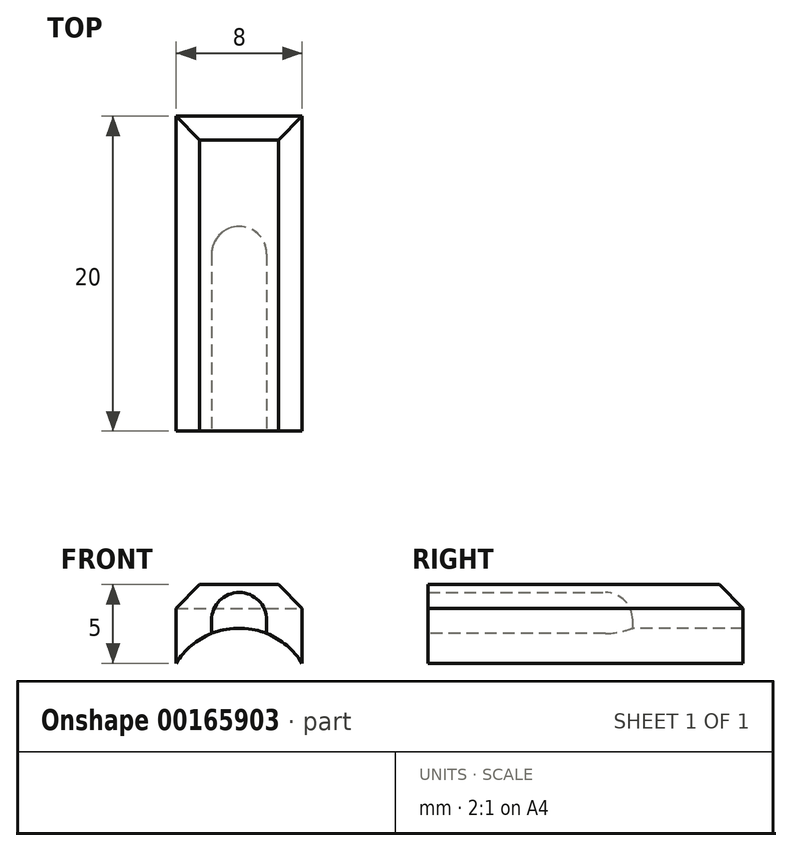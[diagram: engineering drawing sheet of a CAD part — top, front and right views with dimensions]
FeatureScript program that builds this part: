
annotation { "Feature Type Name" : "Feature", "Feature Type Description" : "" }
export const myFeature = defineFeature(function(context is Context, id is Id, definition is map)
    precondition{}
    {
        {
            assignVariable(context, id + "F0", {"name" : "Main_Length", "anyValue" : 20});
        }
        {
            assignVariable(context, id + "F1", {"name" : "Bore_Diam", "anyValue" : 3.5});
        }
        {
            assignVariable(context, id + "F2", {"name" : "Bore_Offset", "anyValue" : 0.5});
        }
        {
            assignVariable(context, id + "F3", {"name" : "Chamfer", "anyValue" : 1.5});
        }
        {
            var Q0;
            Q0=qCreatedBy(makeId("Front.planeOp"),FACE);
            var sketch = newSketch(context, id + "F4", { "sketchPlane" : qUnion([Q0])});
            skArc(sketch, "E0", {"start": v(4, 2.47) * mm, "mid": v(0, 4.7) * mm, "end": v(-4, 2.47) * mm});
            skLineSegment(sketch, "E1.bottom", {"start": v(4, 7.47) * mm, "end": v(-4, 7.47) * mm});
            skLineSegment(sketch, "E1.left", {"start": v(4, 7.47) * mm, "end": v(4, 2.47) * mm});
            skLineSegment(sketch, "E1.right", {"start": v(-4, 7.47) * mm, "end": v(-4, 2.47) * mm});
            skPoint(sketch, "E1.middle", {"position": v(0, 4.97) * mm});
            skArc(sketch, "E2", {"start": v(1.75, 5.22) * mm, "mid": v(0, 6.97) * mm, "end": v(-1.75, 5.22) * mm});
            skLineSegment(sketch, "E3", {"start": v(-1.75, 5.22) * mm, "end": v(-1.75, 4.36) * mm});
            skLineSegment(sketch, "E4", {"start": v(1.75, 5.22) * mm, "end": v(1.75, 4.36) * mm});
            skSolve(sketch);
        }
        {
            var Q0;
            Q0=makeQuery(id+"F4.imprint","IMPRINT",FACE,{"disambiguationData":[TD([[makeQuery(id+"F4.imprint","IMPRINT",EDGE,{"derivedFrom":sQuery(id+"F4.wireOp",EDGE,"E0")}),-1.0]])]});
            var Q1;
            {var subQ0=sQuery(id+"F4.wireOp",EDGE,"E2");var subQ1=sQuery(id+"F4.wireOp",EDGE,"E0");var subQ2=makeQuery(id+"F4.imprint","INTERSECT",VERTEX,{"disambiguationData":[OD(0.0)],"derivedFrom":[subQ1,subQ0]});Q1=makeQuery(id+"F4.imprint","IMPRINT",FACE,{"disambiguationData":[TD([[makeQuery(id+"F4.imprint","IMPRINT",EDGE,{"disambiguationData":[TD([[subQ2,-1.0]])],"derivedFrom":subQ1}),-1.0]])]});}
            var Q2;
            Q2=makeQuery(id+"F4.imprint","IMPRINT",FACE,{"disambiguationData":[TD([[makeQuery(id+"F4.imprint","IMPRINT",EDGE,{"derivedFrom":sQuery(id+"F4.wireOp",EDGE,"E2")}),1.0]])]});
            extrude(context, id + "F5", {"entities" : qUnion([Q0, Q1, Q2]), "oppositeDirection" : true, "depth" : (getVariable(context, 'Main_Length')) * mm});
        }
        {
            var Q0;
            Q0=makeQuery(id+"F5.opExtrude","SWEPT_EDGE",EDGE,{"disambiguationData":[OSD([sQuery(id+"F4.wireOp",EDGE,"E1.bottom"),sQuery(id+"F4.wireOp",EDGE,"E1.right")])]});
            var Q1;
            Q1=makeQuery(id+"F5.opExtrude","SWEPT_EDGE",EDGE,{"disambiguationData":[OSD([sQuery(id+"F4.wireOp",EDGE,"E1.bottom"),sQuery(id+"F4.wireOp",EDGE,"E1.left")])]});
            chamfer(context, id + "F6", {"entities" : qUnion([Q0, Q1]), "width" : (getVariable(context, 'Chamfer')) * mm, "tangentPropagation" : true});
        }
        {
            var Q0;
            Q0=makeQuery(id+"F5.opExtrude","CAP_EDGE",EDGE,{"disambiguationData":[OSD([sQuery(id+"F4.wireOp",EDGE,"E1.bottom")])],"isStart":false});
            chamfer(context, id + "F7", {"entities" : qUnion([Q0]), "width" : 1.5 * mm, "tangentPropagation" : true});
        }
        {
            var Q0;
            Q0=makeQuery(id+"F5.opExtrude","SWEPT_FACE",FACE,{"disambiguationData":[OSD([sQuery(id+"F4.wireOp",EDGE,"E1.bottom")])]});
            cPlane(context, id + "F8", {"entities" : qUnion([Q0]), "cplaneType" : CPlaneType.OFFSET, "offset" : (getVariable(context, 'Bore_Offset') + getVariable(context, 'Bore_Diam') / 2) * mm, "oppositeDirection" : true, "width" : 150 * mm, "height" : 150 * mm});
        }
        {
            var Q0;
            Q0=qCreatedBy(id+"F8.planeOp",FACE);
            var sketch = newSketch(context, id + "F9", { "sketchPlane" : qUnion([Q0])});
            skLineSegment(sketch, "E5", {"start": v(-1.75, 0) * mm, "end": v(-1.75, 11.25) * mm});
            skLineSegment(sketch, "E6", {"start": v(1.75, 0) * mm, "end": v(1.75, 11.25) * mm});
            skArc(sketch, "E7", {"start": v(1.75, 11.25) * mm, "mid": v(0, 13) * mm, "end": v(-1.75, 11.25) * mm});
            skLineSegment(sketch, "E8", {"start": v(-1.75, 0) * mm, "end": v(1.75, 0) * mm});
            skLineSegment(sketch, "E9", {"start": v(0, 0) * mm, "end": v(0, 13) * mm});
            skSolve(sketch);
        }
        {
            var Q0;
            {var subQ0=sQuery(id+"F9.wireOp",EDGE,"E5");Q0=makeQuery(id+"F9.imprint","IMPRINT",FACE,{"disambiguationData":[TD([[makeQuery(id+"F9.imprint","IMPRINT",EDGE,{"derivedFrom":subQ0}),-1.0]])]});}
            var Q1;
            Q1=sQuery(id+"F9.wireOp",EDGE,"E9");
            revolve(context, id + "F10", {"operationType" : NewBodyOperationType.REMOVE, "entities" : qUnion([Q0]), "axis" : qUnion([Q1]), "revolveType" : RevolveType.FULL, "oppositeDirection" : true});
        }
        {
            var Q0;
            {var subQ0=sQuery(id+"F9.wireOp",EDGE,"E6");Q0=makeQuery(id+"F9.imprint","IMPRINT",FACE,{"disambiguationData":[TD([[makeQuery(id+"F9.imprint","IMPRINT",EDGE,{"derivedFrom":subQ0}),1.0]])]});}
            var Q1;
            {var subQ0=sQuery(id+"F9.wireOp",EDGE,"E5");Q1=makeQuery(id+"F9.imprint","IMPRINT",FACE,{"disambiguationData":[TD([[makeQuery(id+"F9.imprint","IMPRINT",EDGE,{"derivedFrom":subQ0}),-1.0]])]});}
            extrude(context, id + "F11", {"entities" : qUnion([Q0, Q1]), "operationType" : NewBodyOperationType.REMOVE, "endBound" : BoundingType.THROUGH_ALL, "oppositeDirection" : true, "depth" : 25 * mm});
        }
    });
